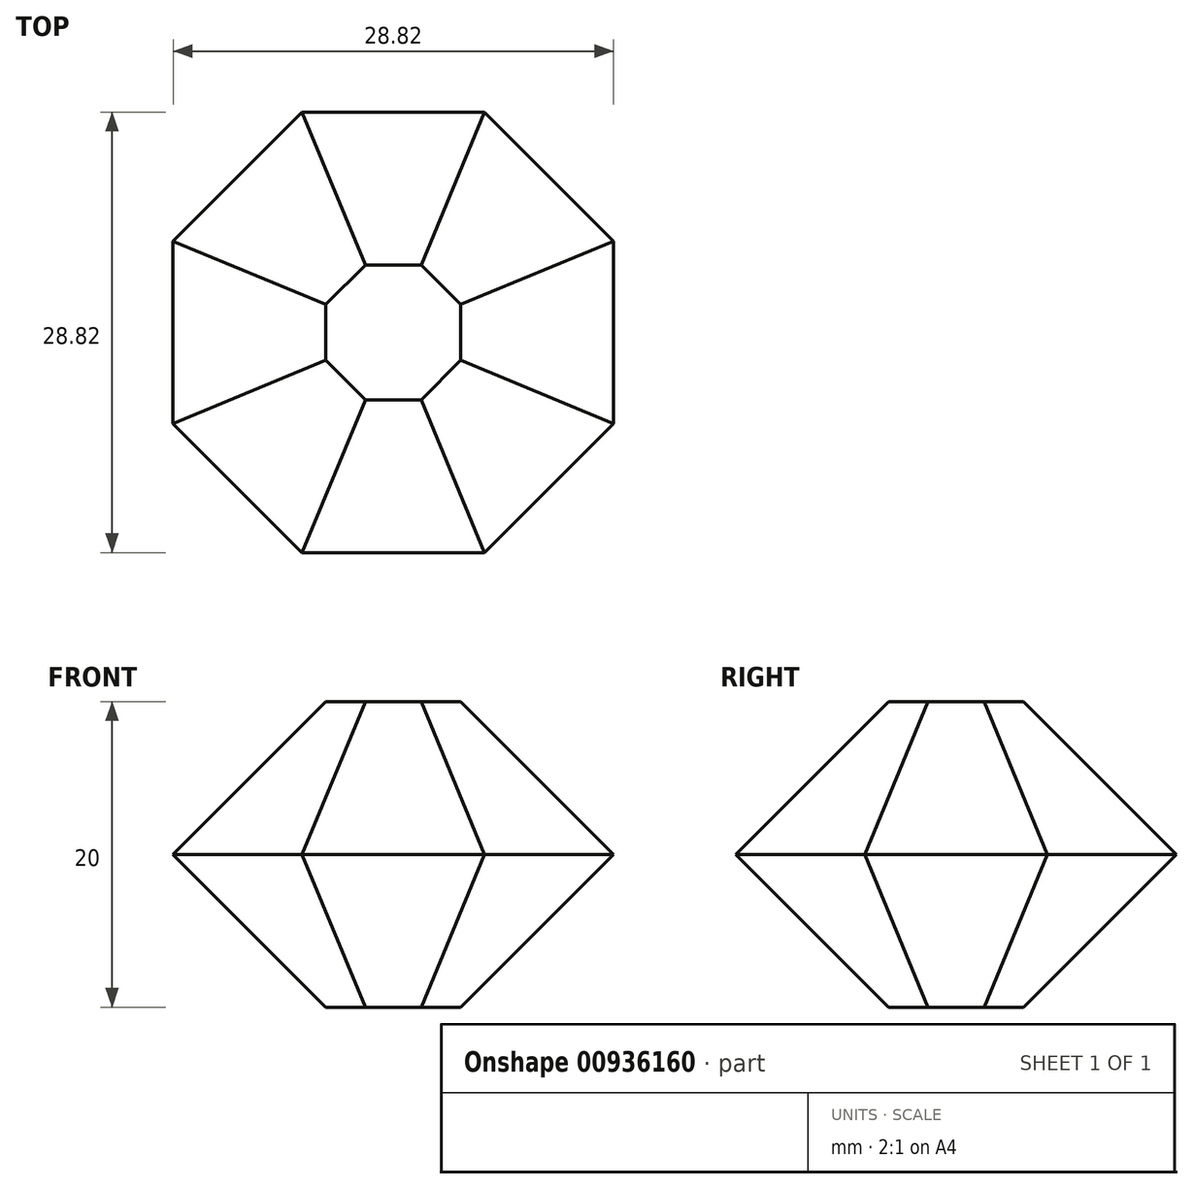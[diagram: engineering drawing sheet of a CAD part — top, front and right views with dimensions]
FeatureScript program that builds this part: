
annotation { "Feature Type Name" : "Feature", "Feature Type Description" : "" }
export const myFeature = defineFeature(function(context is Context, id is Id, definition is map)
    precondition{}
    {
        {
            var Q0;
            Q0=qCreatedBy(makeId("Top.planeOp"),FACE);
            var sketch = newSketch(context, id + "F0", { "sketchPlane" : qUnion([Q0])});
            skCircle(sketch, "E0.cCircle", {"center": v(0, 0) * mm, "radius": 14.41 * mm, "construction": true});
            skLineSegment(sketch, "E0.0", {"start": v(5.97, -14.41) * mm, "end": v(-5.97, -14.41) * mm});
            skLineSegment(sketch, "E0.1", {"start": v(-5.97, -14.41) * mm, "end": v(-14.41, -5.97) * mm});
            skLineSegment(sketch, "E0.2", {"start": v(-14.41, -5.97) * mm, "end": v(-14.41, 5.97) * mm});
            skLineSegment(sketch, "E0.3", {"start": v(-14.41, 5.97) * mm, "end": v(-5.97, 14.41) * mm});
            skLineSegment(sketch, "E0.4", {"start": v(-5.97, 14.41) * mm, "end": v(5.97, 14.41) * mm});
            skLineSegment(sketch, "E0.5", {"start": v(5.97, 14.41) * mm, "end": v(14.41, 5.97) * mm});
            skLineSegment(sketch, "E0.6", {"start": v(14.41, 5.97) * mm, "end": v(14.41, -5.97) * mm});
            skLineSegment(sketch, "E0.7", {"start": v(14.41, -5.97) * mm, "end": v(5.97, -14.41) * mm});
            skPoint(sketch, "E0.0.midPoint", {"position": v(0, -14.41) * mm});
            skLineSegment(sketch, "E1.0", {"start": v(8.32, -14.41) * mm, "end": v(-8.32, -14.41) * mm});
            skLineSegment(sketch, "E1.1", {"start": v(-8.32, -14.41) * mm, "end": v(-16.64, 0) * mm});
            skLineSegment(sketch, "E1.2", {"start": v(-16.64, 0) * mm, "end": v(-8.32, 14.41) * mm});
            skLineSegment(sketch, "E1.3", {"start": v(-8.32, 14.41) * mm, "end": v(8.32, 14.41) * mm});
            skLineSegment(sketch, "E1.4", {"start": v(8.32, 14.41) * mm, "end": v(16.64, 0) * mm});
            skLineSegment(sketch, "E1.5", {"start": v(16.64, 0) * mm, "end": v(8.32, -14.41) * mm});
            skSolve(sketch);
        }
        {
            var Q0;
            Q0=makeQuery(id+"F0.imprint","IMPRINT",FACE,{"disambiguationData":[TD([[makeQuery(id+"F0.imprint","IMPRINT",EDGE,{"derivedFrom":sQuery(id+"F0.wireOp",EDGE,"E0.0")}),-1.0]])]});
            var Q1;
            {var subQ0=sQuery(id+"F0.wireOp",EDGE,"E0.2");var subQ1=sQuery(id+"F0.wireOp",EDGE,"E0.1");var subQ2=makeQuery(id+"F0.imprint","INTERSECT",VERTEX,{"derivedFrom":[subQ1,subQ0]});Q1=makeQuery(id+"F0.imprint","IMPRINT",FACE,{"disambiguationData":[TD([[makeQuery(id+"F0.imprint","IMPRINT",EDGE,{"disambiguationData":[TD([[subQ2,1.0]])],"derivedFrom":subQ1}),-1.0]])]});}
            var Q2;
            {var subQ0=sQuery(id+"F0.wireOp",EDGE,"E0.3");var subQ1=sQuery(id+"F0.wireOp",EDGE,"E0.2");var subQ2=makeQuery(id+"F0.imprint","INTERSECT",VERTEX,{"derivedFrom":[subQ1,subQ0]});Q2=makeQuery(id+"F0.imprint","IMPRINT",FACE,{"disambiguationData":[TD([[makeQuery(id+"F0.imprint","IMPRINT",EDGE,{"disambiguationData":[TD([[subQ2,1.0]])],"derivedFrom":subQ1}),-1.0]])]});}
            var Q3;
            {var subQ0=sQuery(id+"F0.wireOp",EDGE,"E1.5");var subQ1=sQuery(id+"F0.wireOp",EDGE,"E0.6");var subQ2=makeQuery(id+"F0.imprint","INTERSECT",VERTEX,{"derivedFrom":[subQ1,subQ0]});Q3=makeQuery(id+"F0.imprint","IMPRINT",FACE,{"disambiguationData":[TD([[makeQuery(id+"F0.imprint","IMPRINT",EDGE,{"disambiguationData":[TD([[subQ2,-1.0]])],"derivedFrom":subQ1}),-1.0]])]});}
            var Q4;
            {var subQ18=sQuery(id+"F0.wireOp",EDGE,"E0.0");Q4=makeQuery(id+"F0.imprint","IMPRINT",FACE,{"disambiguationData":[TD([[makeQuery(id+"F0.imprint","IMPRINT",EDGE,{"derivedFrom":subQ18}),-1.0]])]});}
            var Q5;
            {var subQ0=sQuery(id+"F0.wireOp",EDGE,"E0.6");var subQ1=sQuery(id+"F0.wireOp",EDGE,"E0.5");var subQ2=makeQuery(id+"F0.imprint","INTERSECT",VERTEX,{"derivedFrom":[subQ1,subQ0]});Q5=makeQuery(id+"F0.imprint","IMPRINT",FACE,{"disambiguationData":[TD([[makeQuery(id+"F0.imprint","IMPRINT",EDGE,{"disambiguationData":[TD([[subQ2,1.0]])],"derivedFrom":subQ1}),-1.0]])]});}
            extrude(context, id + "F1", {"entities" : qUnion([Q0, Q1, Q2, Q3, Q4, Q5]), "depth" : 20 * mm, "offsetDistance" : 25 * mm});
        }
        {
            var Q0;
            Q0=makeQuery(id+"F1.opExtrude","CAP_FACE",FACE,{"disambiguationData":[OSD([sQuery(id+"F0.wireOp",EDGE,"E0.0"),sQuery(id+"F0.wireOp",EDGE,"E0.1"),sQuery(id+"F0.wireOp",EDGE,"E0.2"),sQuery(id+"F0.wireOp",EDGE,"E0.3"),sQuery(id+"F0.wireOp",EDGE,"E0.4"),sQuery(id+"F0.wireOp",EDGE,"E0.5"),sQuery(id+"F0.wireOp",EDGE,"E0.6"),sQuery(id+"F0.wireOp",EDGE,"E0.7")])],"isStart":false});
            var Q1;
            Q1=makeQuery(id+"F1.opExtrude","CAP_FACE",FACE,{"disambiguationData":[OSD([sQuery(id+"F0.wireOp",EDGE,"E0.0"),sQuery(id+"F0.wireOp",EDGE,"E0.1"),sQuery(id+"F0.wireOp",EDGE,"E0.2"),sQuery(id+"F0.wireOp",EDGE,"E0.3"),sQuery(id+"F0.wireOp",EDGE,"E0.4"),sQuery(id+"F0.wireOp",EDGE,"E0.5"),sQuery(id+"F0.wireOp",EDGE,"E0.6"),sQuery(id+"F0.wireOp",EDGE,"E0.7")])],"isStart":true});
            chamfer(context, id + "F2", {"entities" : qUnion([Q0, Q1]), "width" : 10 * mm, "tangentPropagation" : true});
        }
    });
